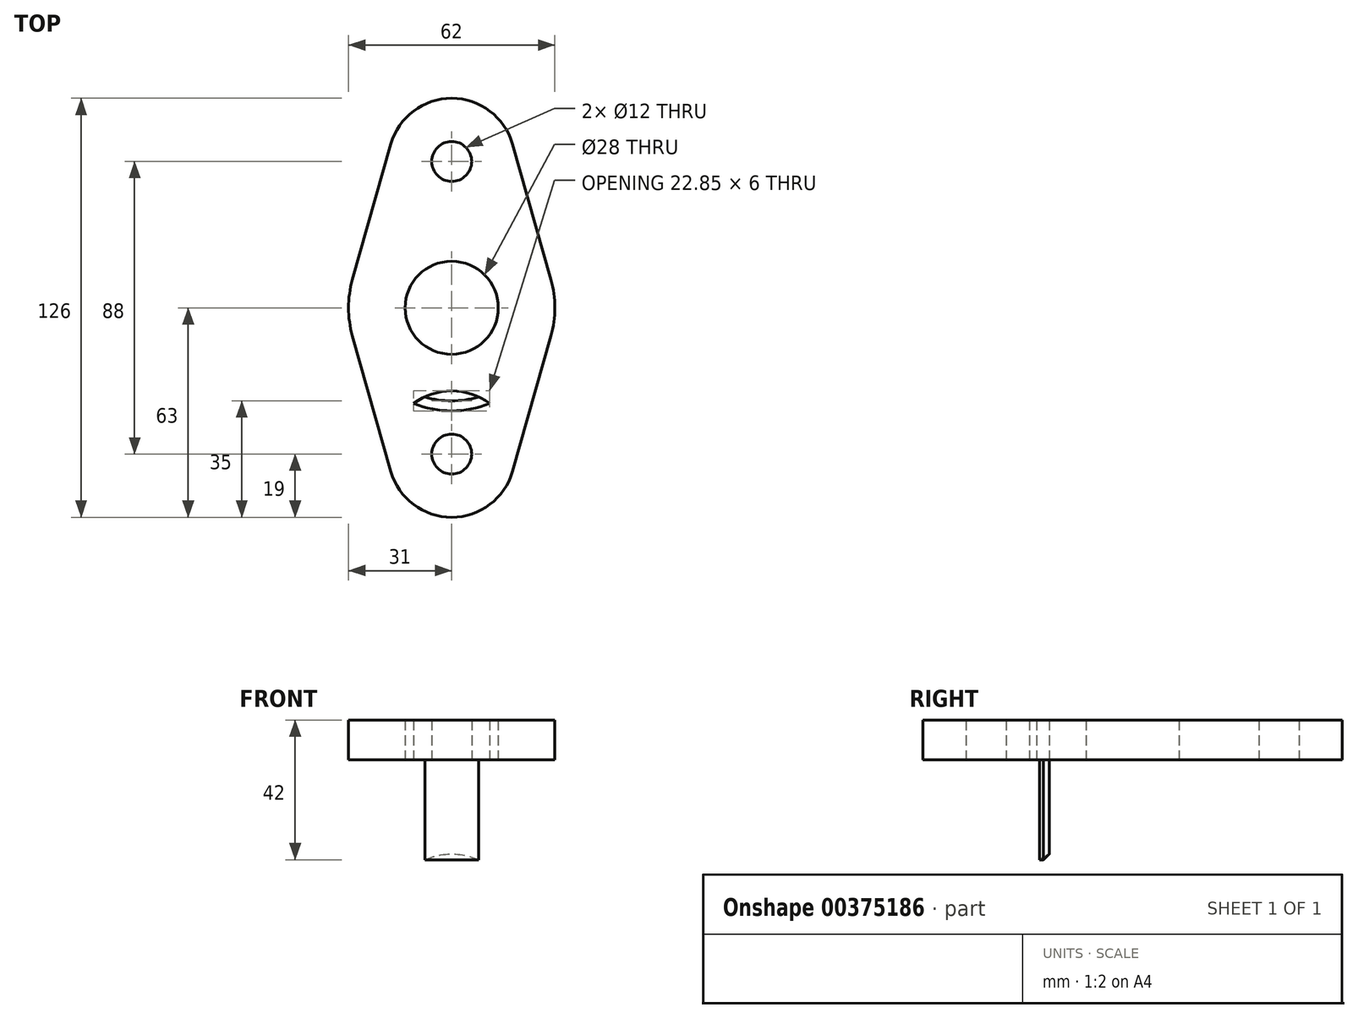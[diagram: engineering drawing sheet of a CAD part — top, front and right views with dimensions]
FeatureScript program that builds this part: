
annotation { "Feature Type Name" : "Feature", "Feature Type Description" : "" }
export const myFeature = defineFeature(function(context is Context, id is Id, definition is map)
    precondition{}
    {
        {
            var Q0;
            Q0=qCreatedBy(makeId("Top.planeOp"),FACE);
            var sketch = newSketch(context, id + "F0", { "sketchPlane" : qUnion([Q0])});
            skCircle(sketch, "E0", {"center": v(0, 44) * mm, "radius": 6 * mm});
            skCircle(sketch, "E1", {"center": v(0, -44) * mm, "radius": 6 * mm});
            skCircle(sketch, "E2", {"center": v(0, 44) * mm, "radius": 19 * mm});
            skCircle(sketch, "E3", {"center": v(0, -44) * mm, "radius": 19 * mm});
            skCircle(sketch, "E4", {"center": v(0, 0) * mm, "radius": 31 * mm});
            skLineSegment(sketch, "E5", {"start": v(18.28, 49.18) * mm, "end": v(29.82, 8.45) * mm});
            skLineSegment(sketch, "E6", {"start": v(29.82, -8.45) * mm, "end": v(18.28, -49.18) * mm});
            skLineSegment(sketch, "E7", {"start": v(-18.28, -49.18) * mm, "end": v(-29.82, -8.45) * mm});
            skLineSegment(sketch, "E8", {"start": v(-29.82, 8.45) * mm, "end": v(-18.28, 49.18) * mm});
            skCircle(sketch, "E9", {"center": v(0, 0) * mm, "radius": 14 * mm});
            skSolve(sketch);
        }
        {
            var Q0;
            Q0=makeQuery(id+"F0.imprint","IMPRINT",FACE,{"disambiguationData":[TD([[makeQuery(id+"F0.imprint","IMPRINT",EDGE,{"derivedFrom":sQuery(id+"F0.wireOp",EDGE,"E0")}),-1.0]])]});
            var Q1;
            {var subQ0=sQuery(id+"F0.wireOp",EDGE,"E8");Q1=makeQuery(id+"F0.imprint","IMPRINT",FACE,{"disambiguationData":[TD([[makeQuery(id+"F0.imprint","IMPRINT",EDGE,{"derivedFrom":subQ0}),-1.0]])]});}
            var Q2;
            {var subQ0=sQuery(id+"F0.wireOp",EDGE,"E5");Q2=makeQuery(id+"F0.imprint","IMPRINT",FACE,{"disambiguationData":[TD([[makeQuery(id+"F0.imprint","IMPRINT",EDGE,{"derivedFrom":subQ0}),-1.0]])]});}
            var Q3;
            {var subQ0=sQuery(id+"F0.wireOp",EDGE,"E4");var subQ1=sQuery(id+"F0.wireOp",EDGE,"E2");var subQ2=makeQuery(id+"F0.imprint","INTERSECT",VERTEX,{"disambiguationData":[OD(0.0)],"derivedFrom":[subQ1,subQ0]});Q3=makeQuery(id+"F0.imprint","IMPRINT",FACE,{"disambiguationData":[TD([[makeQuery(id+"F0.imprint","IMPRINT",EDGE,{"disambiguationData":[TD([[subQ2,-1.0]])],"derivedFrom":subQ1}),1.0]])]});}
            var Q4;
            Q4=makeQuery(id+"F0.imprint","IMPRINT",FACE,{"disambiguationData":[TD([[makeQuery(id+"F0.imprint","IMPRINT",EDGE,{"derivedFrom":sQuery(id+"F0.wireOp",EDGE,"E9")}),-1.0]])]});
            var Q5;
            {var subQ0=sQuery(id+"F0.wireOp",EDGE,"E4");var subQ1=sQuery(id+"F0.wireOp",EDGE,"E3");var subQ2=makeQuery(id+"F0.imprint","INTERSECT",VERTEX,{"disambiguationData":[OD(0.0)],"derivedFrom":[subQ1,subQ0]});Q5=makeQuery(id+"F0.imprint","IMPRINT",FACE,{"disambiguationData":[TD([[makeQuery(id+"F0.imprint","IMPRINT",EDGE,{"disambiguationData":[TD([[subQ2,1.0]])],"derivedFrom":subQ1}),1.0]])]});}
            var Q6;
            {var subQ0=sQuery(id+"F0.wireOp",EDGE,"E7");Q6=makeQuery(id+"F0.imprint","IMPRINT",FACE,{"disambiguationData":[TD([[makeQuery(id+"F0.imprint","IMPRINT",EDGE,{"derivedFrom":subQ0}),-1.0]])]});}
            var Q7;
            {var subQ0=sQuery(id+"F0.wireOp",EDGE,"E6");Q7=makeQuery(id+"F0.imprint","IMPRINT",FACE,{"disambiguationData":[TD([[makeQuery(id+"F0.imprint","IMPRINT",EDGE,{"derivedFrom":subQ0}),-1.0]])]});}
            var Q8;
            Q8=makeQuery(id+"F0.imprint","IMPRINT",FACE,{"disambiguationData":[TD([[makeQuery(id+"F0.imprint","IMPRINT",EDGE,{"derivedFrom":sQuery(id+"F0.wireOp",EDGE,"E1")}),-1.0]])]});
            extrude(context, id + "F1", {"entities" : qUnion([Q0, Q1, Q2, Q3, Q4, Q5, Q6, Q7, Q8]), "depth" : 12 * mm});
        }
        {
            var Q0;
            Q0=makeQuery(id+"F1.opExtrude","CAP_FACE",FACE,{"disambiguationData":[OSD([sQuery(id+"F0.wireOp",EDGE,"E0"),sQuery(id+"F0.wireOp",EDGE,"E1"),sQuery(id+"F0.wireOp",EDGE,"E2"),sQuery(id+"F0.wireOp",EDGE,"E3"),sQuery(id+"F0.wireOp",EDGE,"E4"),sQuery(id+"F0.wireOp",EDGE,"E5"),sQuery(id+"F0.wireOp",EDGE,"E6"),sQuery(id+"F0.wireOp",EDGE,"E7"),sQuery(id+"F0.wireOp",EDGE,"E8"),sQuery(id+"F0.wireOp",EDGE,"E9")])],"isStart":true});
            var sketch = newSketch(context, id + "F2", { "sketchPlane" : qUnion([Q0])});
            skCircle(sketch, "E10", {"center": v(0, 0) * mm, "radius": 28 * mm});
            skSolve(sketch);
        }
        {
            var Q0;
            Q0=makeQuery(id+"F2.imprint","IMPRINT",FACE,{"disambiguationData":[TD([[makeQuery(id+"F2.imprint","IMPRINT",EDGE,{"derivedFrom":sQuery(id+"F2.wireOp",EDGE,"E10")}),1.0]])]});
            extrude(context, id + "F3", {"entities" : qUnion([Q0]), "operationType" : NewBodyOperationType.ADD, "depth" : 30 * mm});
        }
        {
            var Q0;
            Q0=qCreatedBy(makeId("Front.planeOp"),FACE);
            var sketch = newSketch(context, id + "F4", { "sketchPlane" : qUnion([Q0])});
            skLineSegment(sketch, "E11", {"start": v(14, -21.92) * mm, "end": v(14, -30) * mm});
            skLineSegment(sketch, "E12", {"start": v(14, -30) * mm, "end": v(28, -30) * mm});
            skLineSegment(sketch, "E13", {"start": v(28, -30) * mm, "end": v(14, -21.92) * mm});
            skSolve(sketch);
        }
        {
            var Q0;
            Q0 = qSketchRegion(id + "F4", true);
            var Q1;
            Q1=makeQuery(id+"F3.opExtrude","CAP_EDGE",EDGE,{"disambiguationData":[OSD([sQuery(id+"F2.wireOp",EDGE,"E10")])],"isStart":false});
            revolve(context, id + "F5", {"operationType" : NewBodyOperationType.REMOVE, "entities" : qUnion([Q0]), "axis" : qUnion([Q1]), "revolveType" : RevolveType.FULL, "oppositeDirection" : true});
        }
    });
